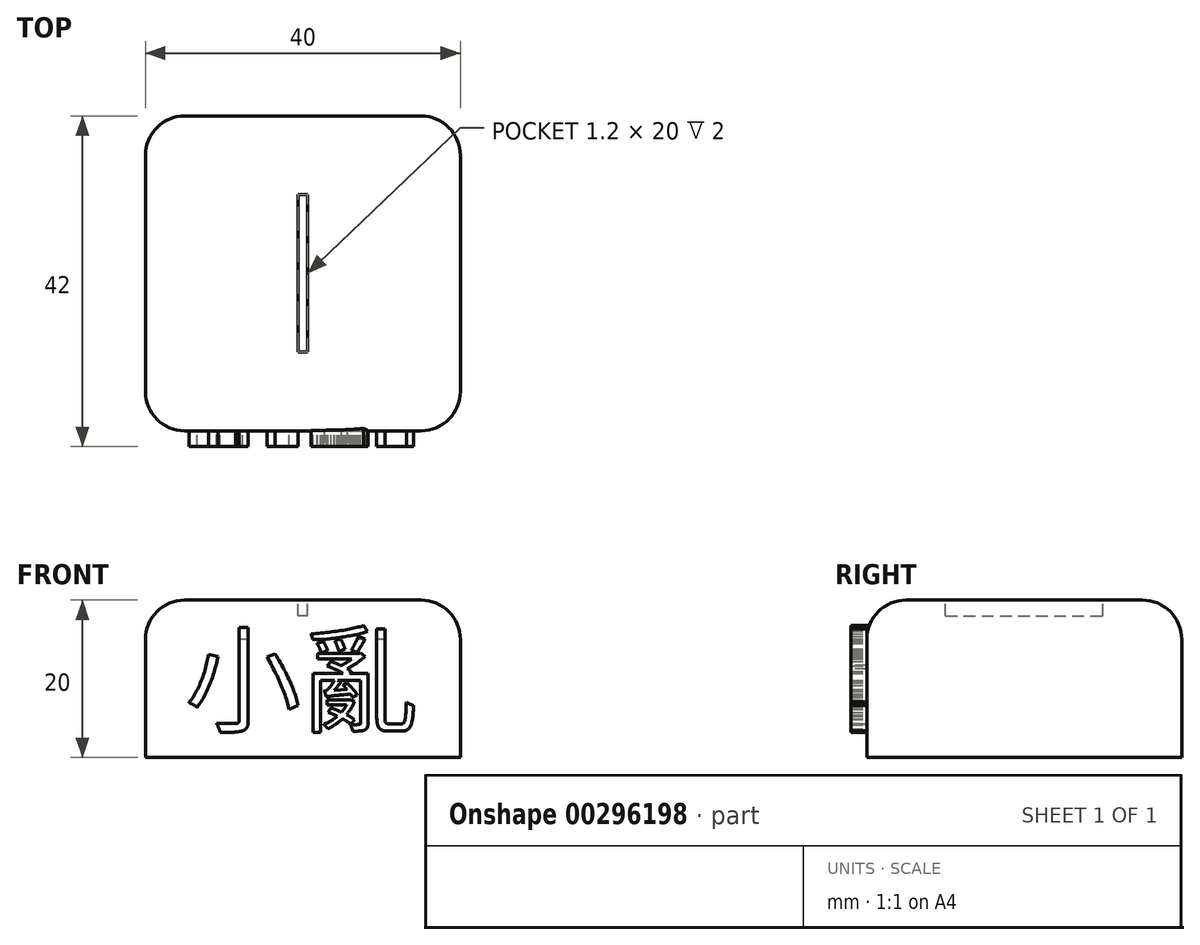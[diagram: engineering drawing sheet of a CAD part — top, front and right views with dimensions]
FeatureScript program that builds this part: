
annotation { "Feature Type Name" : "Feature", "Feature Type Description" : "" }
export const myFeature = defineFeature(function(context is Context, id is Id, definition is map)
    precondition{}
    {
        {
            var Q0;
            Q0=qCreatedBy(makeId("Top.planeOp"),FACE);
            var sketch = newSketch(context, id + "F0", { "sketchPlane" : qUnion([Q0])});
            skLineSegment(sketch, "E0.bottom", {"start": v(20, -20) * mm, "end": v(-20, -20) * mm});
            skLineSegment(sketch, "E0.top", {"start": v(20, 20) * mm, "end": v(-20, 20) * mm});
            skLineSegment(sketch, "E0.left", {"start": v(20, -20) * mm, "end": v(20, 20) * mm});
            skLineSegment(sketch, "E0.right", {"start": v(-20, -20) * mm, "end": v(-20, 20) * mm});
            skPoint(sketch, "E0.middle", {"position": v(0, 0) * mm});
            skLineSegment(sketch, "E1.bottom", {"start": v(0.6, -10) * mm, "end": v(-0.6, -10) * mm});
            skLineSegment(sketch, "E1.top", {"start": v(0.6, 10) * mm, "end": v(-0.6, 10) * mm});
            skLineSegment(sketch, "E1.left", {"start": v(0.6, -10) * mm, "end": v(0.6, 10) * mm});
            skLineSegment(sketch, "E1.right", {"start": v(-0.6, -10) * mm, "end": v(-0.6, 10) * mm});
            skSolve(sketch);
        }
        {
            var Q0;
            Q0=makeQuery(id+"F0.imprint","IMPRINT",FACE,{"disambiguationData":[TD([[makeQuery(id+"F0.imprint","IMPRINT",EDGE,{"derivedFrom":sQuery(id+"F0.wireOp",EDGE,"E0.bottom")}),-1.0]])]});
            var Q1;
            Q1=makeQuery(id+"F0.imprint","IMPRINT",FACE,{"disambiguationData":[TD([[makeQuery(id+"F0.imprint","IMPRINT",EDGE,{"derivedFrom":sQuery(id+"F0.wireOp",EDGE,"E1.bottom")}),-1.0]])]});
            extrude(context, id + "F1", {"entities" : qUnion([Q0, Q1]), "oppositeDirection" : true, "depth" : 20 * mm});
        }
        {
            var Q0;
            Q0=makeQuery(id+"F0.imprint","IMPRINT",FACE,{"disambiguationData":[TD([[makeQuery(id+"F0.imprint","IMPRINT",EDGE,{"derivedFrom":sQuery(id+"F0.wireOp",EDGE,"E1.bottom")}),-1.0]])]});
            extrude(context, id + "F2", {"entities" : qUnion([Q0]), "operationType" : NewBodyOperationType.REMOVE, "oppositeDirection" : true, "depth" : 2 * mm});
        }
        {
            var Q0;
            Q0=makeQuery(id+"F2.boolean.opBoolean","COPY",EDGE,{"derivedFrom":makeQuery(id+"F2.opExtrude","CAP_EDGE",EDGE,{"disambiguationData":[OSD([sQuery(id+"F0.wireOp",EDGE,"E1.left")])],"isStart":true})});
            var Q1;
            Q1=makeQuery(id+"F2.boolean.opBoolean","COPY",EDGE,{"derivedFrom":makeQuery(id+"F2.opExtrude","CAP_EDGE",EDGE,{"disambiguationData":[OSD([sQuery(id+"F0.wireOp",EDGE,"E1.right")])],"isStart":true})});
            var Q2;
            Q2=makeQuery(id+"F1.opExtrude","SWEPT_EDGE",EDGE,{"disambiguationData":[OSD([sQuery(id+"F0.wireOp",EDGE,"E0.bottom"),sQuery(id+"F0.wireOp",EDGE,"E0.left")])]});
            var Q3;
            Q3=makeQuery(id+"F1.opExtrude","SWEPT_EDGE",EDGE,{"disambiguationData":[OSD([sQuery(id+"F0.wireOp",EDGE,"E0.top"),sQuery(id+"F0.wireOp",EDGE,"E0.left")])]});
            var Q4;
            Q4=makeQuery(id+"F1.opExtrude","CAP_EDGE",EDGE,{"disambiguationData":[OSD([sQuery(id+"F0.wireOp",EDGE,"E0.left")])],"isStart":true});
            var Q5;
            Q5=makeQuery(id+"F1.opExtrude","SWEPT_EDGE",EDGE,{"disambiguationData":[OSD([sQuery(id+"F0.wireOp",EDGE,"E0.bottom"),sQuery(id+"F0.wireOp",EDGE,"E0.right")])]});
            var Q6;
            Q6=makeQuery(id+"F1.opExtrude","SWEPT_EDGE",EDGE,{"disambiguationData":[OSD([sQuery(id+"F0.wireOp",EDGE,"E0.top"),sQuery(id+"F0.wireOp",EDGE,"E0.right")])]});
            var Q7;
            Q7=makeQuery(id+"F1.opExtrude","CAP_EDGE",EDGE,{"disambiguationData":[OSD([sQuery(id+"F0.wireOp",EDGE,"E0.top")])],"isStart":true});
            var Q8;
            Q8=makeQuery(id+"F1.opExtrude","CAP_EDGE",EDGE,{"disambiguationData":[OSD([sQuery(id+"F0.wireOp",EDGE,"E0.right")])],"isStart":true});
            var Q9;
            Q9=makeQuery(id+"F1.opExtrude","CAP_EDGE",EDGE,{"disambiguationData":[OSD([sQuery(id+"F0.wireOp",EDGE,"E0.bottom")])],"isStart":true});
            fillet(context, id + "F3", {"entities" : qUnion([Q0, Q1, Q2, Q3, Q4, Q5, Q6, Q7, Q8, Q9]), "radius" : 5 * mm, "tangentPropagation" : true, "allowEdgeOverflow" : false});
        }
        {
            var Q0;
            Q0=makeQuery(id+"F1.opExtrude","SWEPT_FACE",FACE,{"disambiguationData":[OSD([sQuery(id+"F0.wireOp",EDGE,"E0.bottom")])]});
            var sketch = newSketch(context, id + "F4", { "sketchPlane" : qUnion([Q0])});
            skText(sketch, "E2", { "text": "小亂", "fontName": "NotoSansCJKtc-Regular.otf"});
            const initialGuessF4  = {"E2": [-0.015, -0.01568, 1, 0, 0.01068]};
            skSetInitialGuess(sketch, initialGuessF4);
            skSolve(sketch);
        }
        {
            var Q0;
            {var subQ0=sQuery(id+"F4.wireOp",EDGE,"E2.sketch_text.stroke-1");Q0=makeQuery(id+"F4.imprint","IMPRINT",FACE,{"disambiguationData":[TD([[makeQuery(id+"F4.imprint","IMPRINT",EDGE,{"derivedFrom":subQ0}),1.0]])]});}
            var Q1;
            {var subQ0=sQuery(id+"F4.wireOp",EDGE,"E2.sketch_text.stroke-7");Q1=makeQuery(id+"F4.imprint","IMPRINT",FACE,{"disambiguationData":[TD([[makeQuery(id+"F4.imprint","IMPRINT",EDGE,{"derivedFrom":subQ0}),1.0]])]});}
            var Q2;
            Q2=makeQuery(id+"F4.imprint","IMPRINT",FACE,{"disambiguationData":[TD([[makeQuery(id+"F4.imprint","IMPRINT",EDGE,{"derivedFrom":sQuery(id+"F4.wireOp",EDGE,"E2.sketch_text.stroke-12")}),1.0]])]});
            var Q3;
            Q3=makeQuery(id+"F4.imprint","IMPRINT",FACE,{"disambiguationData":[TD([[makeQuery(id+"F4.imprint","IMPRINT",EDGE,{"derivedFrom":sQuery(id+"F4.wireOp",EDGE,"E2.sketch_text.stroke-8")}),1.0]])]});
            var Q4;
            Q4=makeQuery(id+"F4.imprint","IMPRINT",FACE,{"disambiguationData":[TD([[makeQuery(id+"F4.imprint","IMPRINT",EDGE,{"derivedFrom":sQuery(id+"F4.wireOp",EDGE,"E2.sketch_text.stroke-48")}),1.0]])]});
            var Q5;
            {var subQ0=sQuery(id+"F4.wireOp",EDGE,"E2.sketch_text.stroke-26");Q5=makeQuery(id+"F4.imprint","IMPRINT",FACE,{"disambiguationData":[TD([[makeQuery(id+"F4.imprint","IMPRINT",EDGE,{"derivedFrom":subQ0}),1.0]])]});}
            var Q6;
            Q6=makeQuery(id+"F4.imprint","IMPRINT",FACE,{"disambiguationData":[TD([[makeQuery(id+"F4.imprint","IMPRINT",EDGE,{"derivedFrom":sQuery(id+"F4.wireOp",EDGE,"E2.sketch_text.stroke-28")}),1.0]])]});
            var Q7;
            {var subQ0=sQuery(id+"F4.wireOp",EDGE,"E2.sketch_text.stroke-23");Q7=makeQuery(id+"F4.imprint","IMPRINT",FACE,{"disambiguationData":[TD([[makeQuery(id+"F4.imprint","IMPRINT",EDGE,{"derivedFrom":subQ0}),1.0]])]});}
            var Q8;
            {var subQ0=sQuery(id+"F4.wireOp",EDGE,"E2.sketch_text.stroke-21");Q8=makeQuery(id+"F4.imprint","IMPRINT",FACE,{"disambiguationData":[TD([[makeQuery(id+"F4.imprint","IMPRINT",EDGE,{"derivedFrom":subQ0}),1.0]])]});}
            var Q9;
            Q9=makeQuery(id+"F4.imprint","IMPRINT",FACE,{"disambiguationData":[TD([[makeQuery(id+"F4.imprint","IMPRINT",EDGE,{"derivedFrom":sQuery(id+"F4.wireOp",EDGE,"E2.sketch_text.stroke-32")}),1.0]])]});
            var Q10;
            {var subQ2=sQuery(id+"F4.wireOp",EDGE,"E2.sketch_text.stroke-86");Q10=makeQuery(id+"F4.imprint","IMPRINT",FACE,{"disambiguationData":[TD([[makeQuery(id+"F4.imprint","IMPRINT",EDGE,{"derivedFrom":subQ2}),1.0]])]});}
            var Q11;
            {var subQ0=sQuery(id+"F4.wireOp",EDGE,"E2.sketch_text.stroke-88");Q11=makeQuery(id+"F4.imprint","IMPRINT",FACE,{"disambiguationData":[TD([[makeQuery(id+"F4.imprint","IMPRINT",EDGE,{"derivedFrom":subQ0}),1.0]])]});}
            extrude(context, id + "F5", {"entities" : qUnion([Q0, Q1, Q2, Q3, Q4, Q5, Q6, Q7, Q8, Q9, Q10, Q11]), "operationType" : NewBodyOperationType.ADD, "depth" : 2 * mm});
        }
        {
            var Q0;
            {var subQ6=sQuery(id+"F4.wireOp",EDGE,"E2.sketch_text.stroke-16");Q0=makeQuery(id+"F4.imprint","IMPRINT",FACE,{"disambiguationData":[TD([[makeQuery(id+"F4.imprint","IMPRINT",EDGE,{"derivedFrom":subQ6}),1.0]])]});}
            extrude(context, id + "F6", {"entities" : qUnion([Q0]), "operationType" : NewBodyOperationType.ADD, "endBound" : BoundingType.SYMMETRIC, "depth" : 4 * mm});
        }
    });
